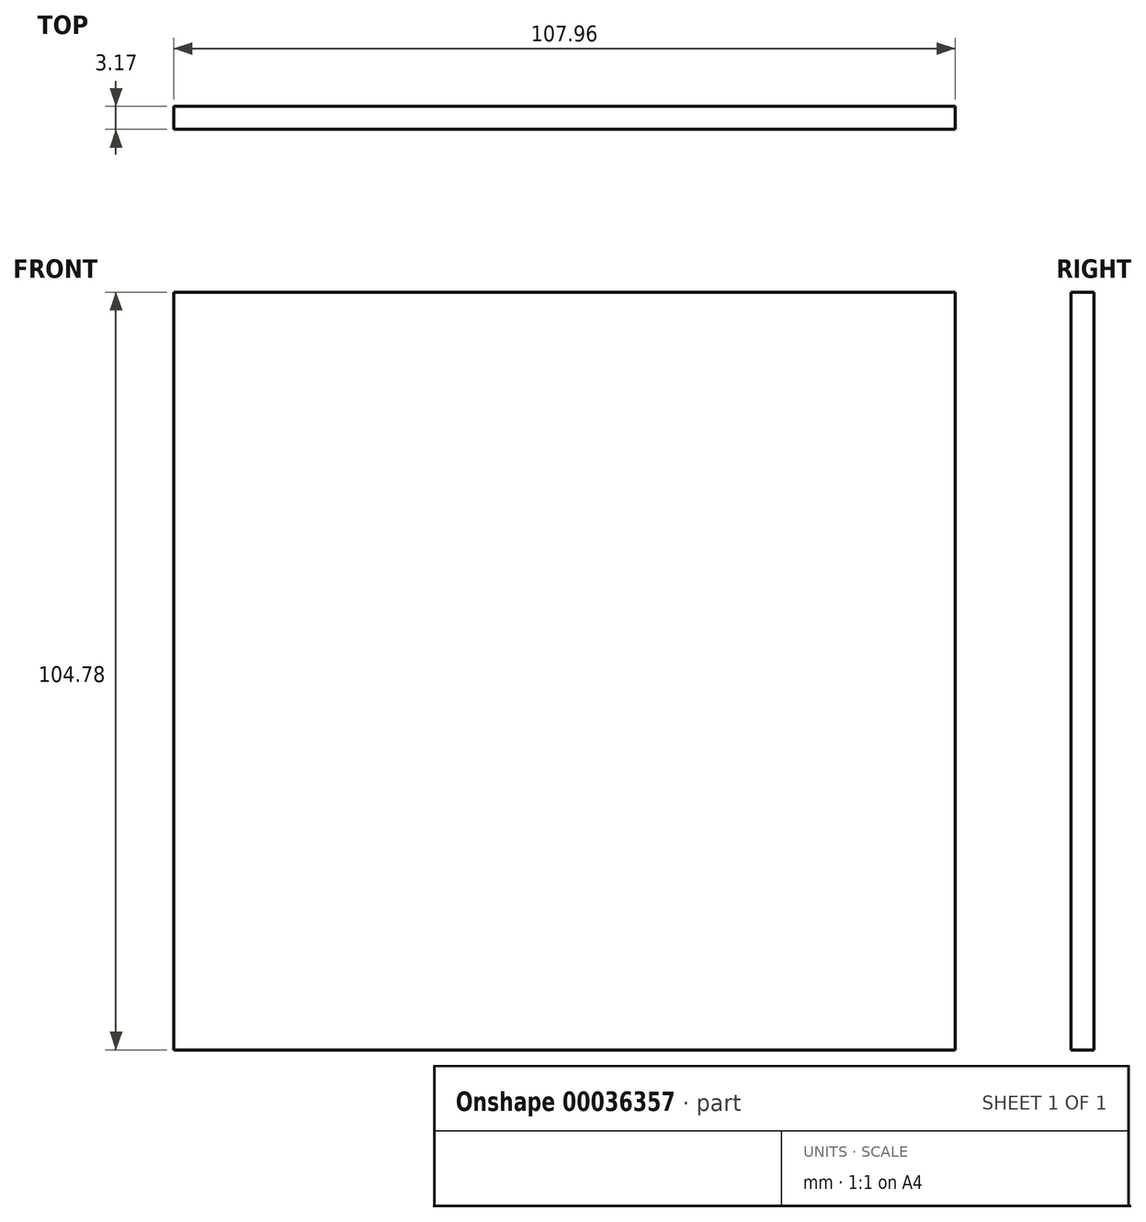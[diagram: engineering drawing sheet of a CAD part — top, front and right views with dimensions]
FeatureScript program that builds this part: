
annotation { "Feature Type Name" : "Feature", "Feature Type Description" : "" }
export const myFeature = defineFeature(function(context is Context, id is Id, definition is map)
    precondition{}
    {
        {
            var Q0;
            Q0=qCreatedBy(makeId("Front.planeOp"),FACE);
            var sketch = newSketch(context, id + "F0", { "sketchPlane" : qUnion([Q0])});
            skLineSegment(sketch, "E0.rect.bottom", {"start": v(-53.97, 52.39) * mm, "end": v(53.98, 52.39) * mm});
            skLineSegment(sketch, "E0.rect.top", {"start": v(-53.98, -52.39) * mm, "end": v(53.97, -52.39) * mm});
            skLineSegment(sketch, "E0.rect.left", {"start": v(-53.97, 52.39) * mm, "end": v(-53.98, -52.39) * mm});
            skLineSegment(sketch, "E0.rect.right", {"start": v(53.98, 52.39) * mm, "end": v(53.97, -52.39) * mm});
            skPoint(sketch, "E0.rect.middle", {"position": v(0, 0) * mm});
            skSolve(sketch);
        }
        {
            var Q0;
            Q0=makeQuery(id+"F0.imprint","IMPRINT",FACE,{"disambiguationData":[TD([[makeQuery(id+"F0.imprint","IMPRINT",EDGE,{"derivedFrom":sQuery(id+"F0.wireOp",EDGE,"E0.rect.bottom")}),-1.0]])]});
            extrude(context, id + "F1", {"entities" : qUnion([Q0]), "depth" : 3.17 * mm});
        }
    });
